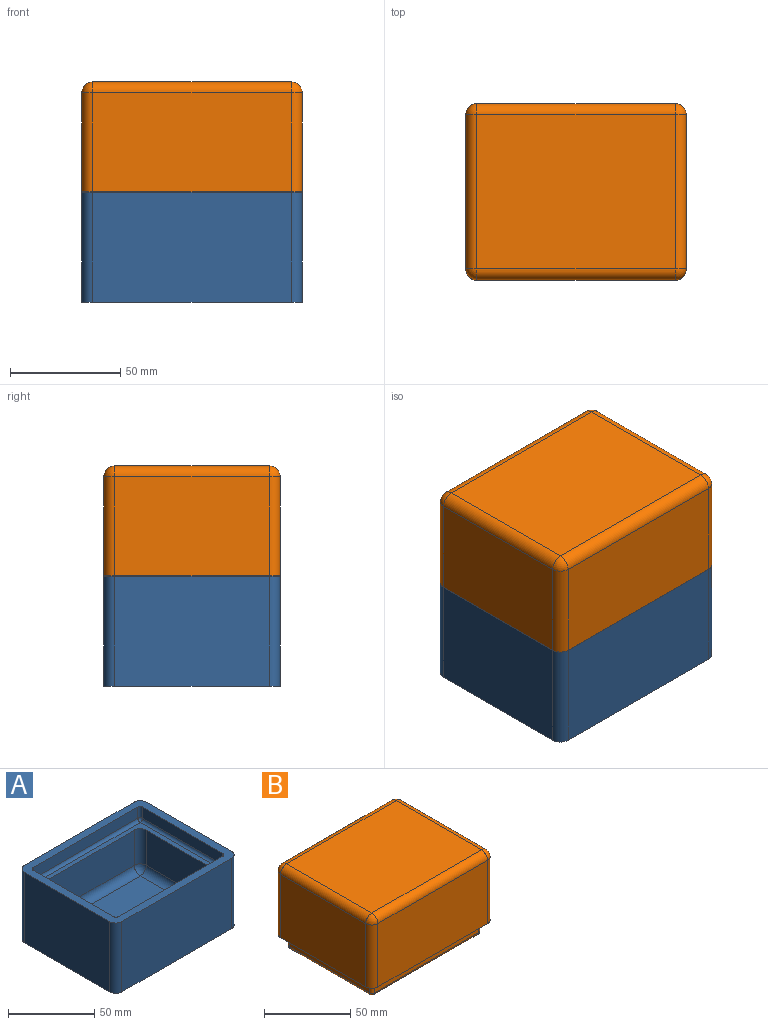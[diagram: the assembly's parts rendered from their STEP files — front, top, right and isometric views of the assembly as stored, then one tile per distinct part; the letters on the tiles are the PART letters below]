
ASSEMBLY  parts=2 mates=1
PART A: 44 faces, bbox 100x80x50 mm
  f0: plane 100x80mm, normal (0,0,1), area 1682mm2, adj f1,f2,f3,f4,f6,f7,f8,f9
  f1: plane 90x50mm, normal (0,-1,0), area 4500mm2, adj f0,f5,f16,f19
  f2: plane 70x50mm, normal (1,0,0), area 3500mm2, adj f0,f5,f16,f17
  f3: plane 90x50mm, normal (0,1,0), area 4500mm2, adj f0,f5,f17,f18
  f4: plane 70x50mm, normal (-1,0,0), area 3500mm2, adj f0,f5,f18,f19
  f5: plane 100x80mm, normal (0,0,-1), area 7978.5mm2, adj f1,f2,f3,f4,f16,f17,f18,f19
  f6: plane 86x8mm, normal (0,1,0), area 688mm2, adj f0,f22,f28,f31
  f7: plane 66x8mm, normal (-1,0,0), area 528mm2, adj f0,f25,f29,f31
  f8: plane 86x8mm, normal (0,-1,0), area 688mm2, adj f0,f20,f24,f25
  f9: plane 66x8mm, normal (1,0,0), area 528mm2, adj f0,f20,f22,f23
  f10: plane 86x66mm, normal (0,0,1), area 897.5mm2, adj f12,f13,f14,f15,f23,f24,f28,f29
  f11: plane 70x50mm, normal (0,0,1), area 3500mm2, adj f35,f36,f40,f41
  f12: plane 50x25mm, normal (1,0,0), area 1250mm2, adj f10,f37,f41,f43
  f13: plane 70x25mm, normal (0,-1,0), area 1750mm2, adj f10,f34,f40,f43
  f14: plane 50x25mm, normal (-1,0,0), area 1250mm2, adj f10,f32,f34,f35
  f15: plane 70x25mm, normal (0,1,0), area 1750mm2, adj f10,f32,f36,f37
  f16: cylinder r=5mm len=50mm, axis (0,0,1), area 392.7mm2, adj f0,f1,f2,f5
  f17: cylinder r=5mm len=50mm, axis (0,0,-1), area 392.7mm2, adj f0,f2,f3,f5
  f18: cylinder r=5mm len=50mm, axis (0,0,1), area 392.7mm2, adj f0,f3,f4,f5
  f19: cylinder r=5mm len=50mm, axis (0,0,-1), area 392.7mm2, adj f0,f1,f4,f5
  f20: cylinder r=2mm len=8mm, axis (0,0,1), area 25.1mm2, adj f0,f8,f9,f21
  f21: sphere r=2mm, area 6.3mm2, adj f20,f23,f24
  f22: cylinder r=2mm len=8mm, axis (0,0,-1), area 25.1mm2, adj f0,f6,f9,f26
  f23: cylinder r=2mm len=66mm, axis (0,-1,0), area 207.3mm2, adj f9,f10,f21,f26
  f24: cylinder r=2mm len=86mm, axis (-1,0,0), area 270.2mm2, adj f8,f10,f21,f27
  f25: cylinder r=2mm len=8mm, axis (0,0,-1), area 25.1mm2, adj f0,f7,f8,f27
  f26: sphere r=2mm, area 6.3mm2, adj f22,f23,f28
  f27: sphere r=2mm, area 6.3mm2, adj f24,f25,f29
  f28: cylinder r=2mm len=86mm, axis (1,0,0), area 270.2mm2, adj f6,f10,f26,f30
  f29: cylinder r=2mm len=66mm, axis (0,1,0), area 207.3mm2, adj f7,f10,f27,f30
  f30: sphere r=2mm, area 6.3mm2, adj f28,f29,f31
  f31: cylinder r=2mm len=8mm, axis (0,0,1), area 25.1mm2, adj f0,f6,f7,f30
  f32: cylinder r=5mm len=25mm, axis (0,0,-1), area 196.3mm2, adj f10,f14,f15,f33
  f33: sphere r=5mm, area 39.3mm2, adj f32,f35,f36
  f34: cylinder r=5mm len=25mm, axis (0,0,1), area 196.3mm2, adj f10,f13,f14,f38
  f35: cylinder r=5mm len=50mm, axis (0,-1,0), area 392.7mm2, adj f11,f14,f33,f38
  f36: cylinder r=5mm len=70mm, axis (-1,0,0), area 549.8mm2, adj f11,f15,f33,f39
  f37: cylinder r=5mm len=25mm, axis (0,0,1), area 196.3mm2, adj f10,f12,f15,f39
  f38: sphere r=5mm, area 39.3mm2, adj f34,f35,f40
  f39: sphere r=5mm, area 39.3mm2, adj f36,f37,f41
  f40: cylinder r=5mm len=70mm, axis (1,0,0), area 549.8mm2, adj f11,f13,f38,f42
  f41: cylinder r=5mm len=50mm, axis (0,1,0), area 392.7mm2, adj f11,f12,f39,f42
  f42: sphere r=5mm, area 39.3mm2, adj f40,f41,f43
  f43: cylinder r=5mm len=25mm, axis (0,0,-1), area 196.3mm2, adj f10,f12,f13,f42
PART B: 60 faces, bbox 100x80x59.9 mm
  f0: plane 85.9x65.9mm, normal (0,0,-1), area 882.3mm2, adj f11,f12,f13,f14,f32,f33,f34,f35
  f1: plane 100x80mm, normal (0,0,-1), area 1039.3mm2, adj f2,f4,f5,f6,f16,f18,f21,f24
  f2: plane 90x45mm, normal (0,1,0), area 4050mm2, adj f1,f21,f24,f27
  f3: plane 90x70mm, normal (0,0,1), area 6300mm2, adj f17,f22,f23,f27
  f4: plane 90x45mm, normal (0,-1,0), area 4050mm2, adj f1,f16,f17,f18
  f5: plane 70x45mm, normal (1,0,0), area 3150mm2, adj f1,f16,f21,f22
  f6: plane 70x45mm, normal (-1,0,0), area 3150mm2, adj f1,f18,f23,f24
  f7: plane 85.9x5.9mm, normal (0,1,0), area 506.8mm2, adj f31,f32,f55,f58
  f8: plane 85.9x5.9mm, normal (0,-1,0), area 506.8mm2, adj f28,f35,f49,f52
  f9: plane 65.9x5.9mm, normal (1,0,0), area 388.8mm2, adj f29,f33,f49,f55
  f10: plane 65.9x5.9mm, normal (-1,0,0), area 388.8mm2, adj f30,f34,f52,f58
  f11: plane 70x40mm, normal (0,-1,0), area 2800mm2, adj f0,f38,f44,f47
  f12: plane 50x40mm, normal (-1,0,0), area 2000mm2, adj f0,f41,f45,f47
  f13: plane 70x40mm, normal (0,1,0), area 2800mm2, adj f0,f36,f40,f41
  f14: plane 50x40mm, normal (1,0,0), area 2000mm2, adj f0,f36,f38,f39
  f15: plane 70x50mm, normal (0,0,-1), area 3500mm2, adj f39,f40,f44,f45
  f16: cylinder r=5mm len=45mm, axis (0,0,1), area 353.4mm2, adj f1,f4,f5,f19
  f17: cylinder r=5mm len=90mm, axis (1,0,0), area 706.9mm2, adj f3,f4,f19,f20
  f18: cylinder r=5mm len=45mm, axis (0,0,-1), area 353.4mm2, adj f1,f4,f6,f20
  f19: sphere r=5mm, area 39.3mm2, adj f16,f17,f22
  f20: sphere r=5mm, area 39.3mm2, adj f17,f18,f23
  f21: cylinder r=5mm len=45mm, axis (0,0,-1), area 353.4mm2, adj f1,f2,f5,f25
  f22: cylinder r=5mm len=70mm, axis (0,1,0), area 549.8mm2, adj f3,f5,f19,f25
  f23: cylinder r=5mm len=70mm, axis (0,-1,0), area 549.8mm2, adj f3,f6,f20,f26
  f24: cylinder r=5mm len=45mm, axis (0,0,1), area 353.4mm2, adj f1,f2,f6,f26
  f25: sphere r=5mm, area 39.3mm2, adj f21,f22,f27
  f26: sphere r=5mm, area 39.3mm2, adj f23,f24,f27
  f27: cylinder r=5mm len=90mm, axis (-1,0,0), area 706.9mm2, adj f2,f3,f25,f26
  f28: cylinder r=2mm len=93.9mm, axis (1,0,0), area 279mm2, adj f1,f8,f48,f51
  f29: cylinder r=2mm len=73.9mm, axis (0,1,0), area 216.2mm2, adj f1,f9,f48,f56
  f30: cylinder r=2mm len=73.9mm, axis (0,-1,0), area 216.2mm2, adj f1,f10,f51,f59
  f31: cylinder r=2mm len=93.9mm, axis (1,0,0), area 279mm2, adj f1,f7,f56,f59
  f32: cylinder r=2mm len=85.9mm, axis (-1,0,0), area 269.9mm2, adj f0,f7,f54,f57
  f33: cylinder r=2mm len=65.9mm, axis (0,-1,0), area 207mm2, adj f0,f9,f50,f54
  f34: cylinder r=2mm len=65.9mm, axis (0,1,0), area 207mm2, adj f0,f10,f53,f57
  f35: cylinder r=2mm len=85.9mm, axis (-1,0,0), area 269.9mm2, adj f0,f8,f50,f53
  f36: cylinder r=5mm len=40mm, axis (0,0,-1), area 314.2mm2, adj f0,f13,f14,f37
  f37: sphere r=5mm, area 39.3mm2, adj f36,f39,f40
  f38: cylinder r=5mm len=40mm, axis (0,0,1), area 314.2mm2, adj f0,f11,f14,f42
  f39: cylinder r=5mm len=50mm, axis (0,1,0), area 392.7mm2, adj f14,f15,f37,f42
  f40: cylinder r=5mm len=70mm, axis (-1,0,0), area 549.8mm2, adj f13,f15,f37,f43
  f41: cylinder r=5mm len=40mm, axis (0,0,1), area 314.2mm2, adj f0,f12,f13,f43
  f42: sphere r=5mm, area 39.3mm2, adj f38,f39,f44
  f43: sphere r=5mm, area 39.3mm2, adj f40,f41,f45
  f44: cylinder r=5mm len=70mm, axis (1,0,0), area 549.8mm2, adj f11,f15,f42,f46
  f45: cylinder r=5mm len=50mm, axis (0,-1,0), area 392.7mm2, adj f12,f15,f43,f46
  f46: sphere r=5mm, area 39.3mm2, adj f44,f45,f47
  f47: cylinder r=5mm len=40mm, axis (0,0,-1), area 314.2mm2, adj f0,f11,f12,f46
  f48: bspline ~4x4mm, area 7.6mm2, adj f28,f29,f49
  f49: cylinder r=2mm len=5.9mm, axis (0,0,1), area 18.5mm2, adj f8,f9,f48,f50
  f50: sphere r=2mm, area 6.3mm2, adj f33,f35,f49
  f51: bspline ~4x4mm, area 7.6mm2, adj f28,f30,f52
  f52: cylinder r=2mm len=5.9mm, axis (0,0,-1), area 18.5mm2, adj f8,f10,f51,f53
  f53: sphere r=2mm, area 6.3mm2, adj f34,f35,f52
  f54: sphere r=2mm, area 6.3mm2, adj f32,f33,f55
  f55: cylinder r=2mm len=5.9mm, axis (0,0,-1), area 18.5mm2, adj f7,f9,f54,f56
  f56: bspline ~4x4mm, area 7.6mm2, adj f29,f31,f55
  f57: sphere r=2mm, area 6.3mm2, adj f32,f34,f58
  f58: cylinder r=2mm len=5.9mm, axis (0,0,1), area 18.5mm2, adj f7,f10,f57,f59
  f59: bspline ~4x4mm, area 7.6mm2, adj f30,f31,f58
PLACE A t=(0,0,-40)mm fixed
PLACE B t=(0,0,-40.1)mm
MATE slider B.f0 <-> A.f10  axis (0,0,1) through (0,0,0)mm
